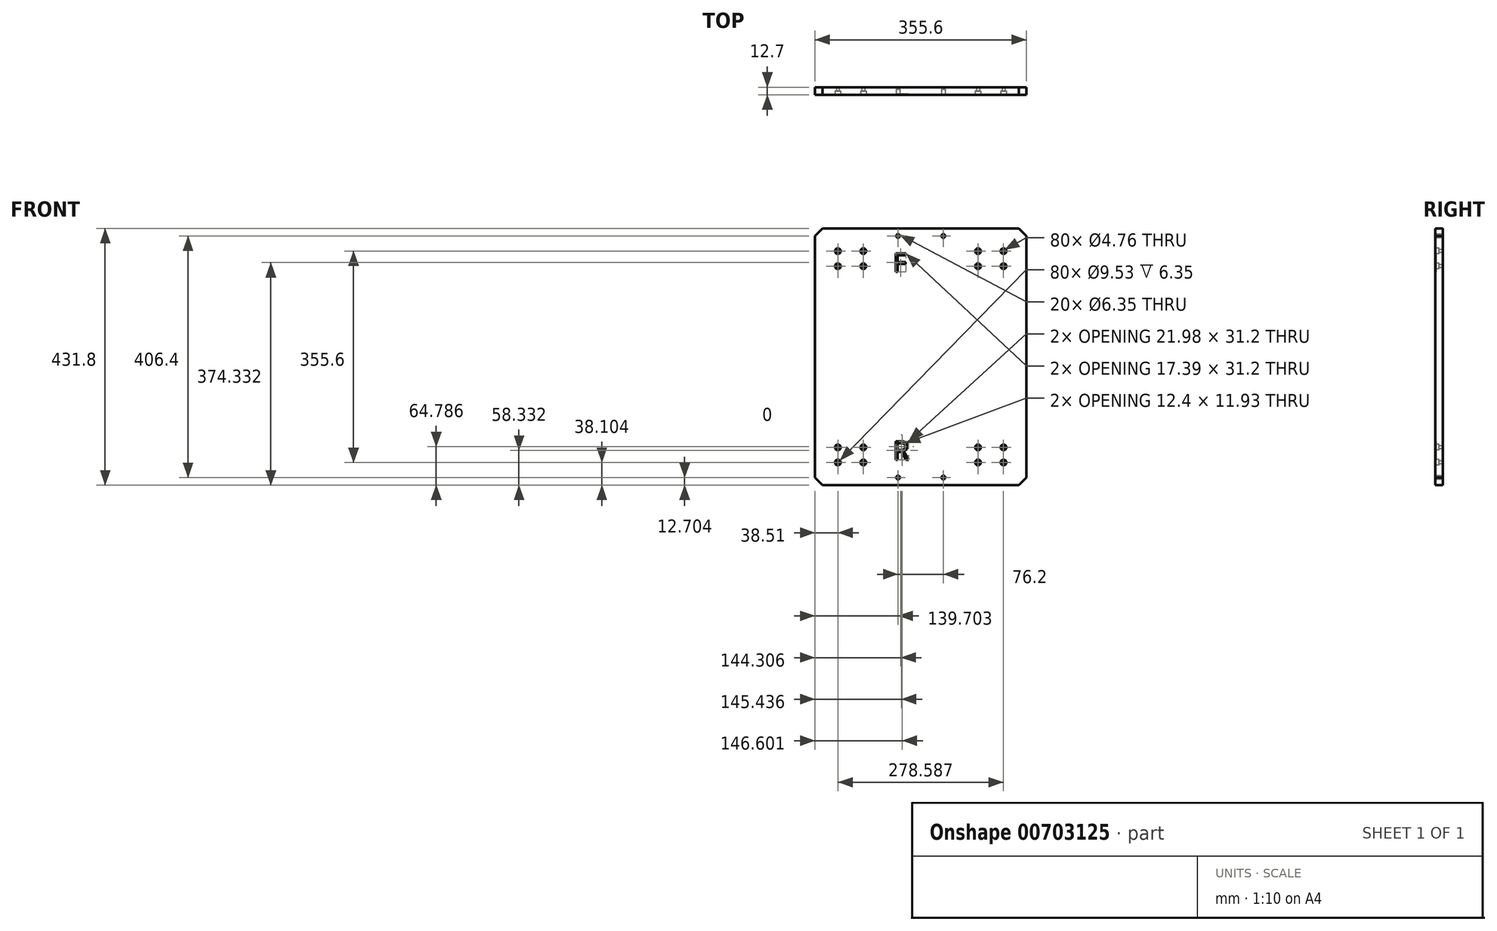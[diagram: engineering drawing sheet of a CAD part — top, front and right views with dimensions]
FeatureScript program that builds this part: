
annotation { "Feature Type Name" : "Feature", "Feature Type Description" : "" }
export const myFeature = defineFeature(function(context is Context, id is Id, definition is map)
    precondition{}
    {
        {
            var Q0;
            Q0=qCreatedBy(makeId("Front.planeOp"),FACE);
            var sketch = newSketch(context, id + "F0", { "sketchPlane" : qUnion([Q0])});
            skLineSegment(sketch, "E0.bottom", {"start": v(-223.94, -202.15) * mm, "end": v(131.66, -202.15) * mm});
            skLineSegment(sketch, "E0.top", {"start": v(-223.94, 229.65) * mm, "end": v(131.66, 229.65) * mm});
            skLineSegment(sketch, "E0.left", {"start": v(-223.94, -202.15) * mm, "end": v(-223.94, 229.65) * mm});
            skLineSegment(sketch, "E0.right", {"start": v(131.66, -202.15) * mm, "end": v(131.66, 229.65) * mm});
            skSolve(sketch);
        }
        {
            var Q0;
            Q0=makeQuery(id+"F0.imprint","IMPRINT",FACE,{"disambiguationData":[TD([[makeQuery(id+"F0.imprint","IMPRINT",EDGE,{"derivedFrom":sQuery(id+"F0.wireOp",EDGE,"E0.bottom")}),1.0]])]});
            extrude(context, id + "F1", {"entities" : qUnion([Q0]), "depth" : 12.7 * mm, "offsetDistance" : 25.4 * mm});
        }
        {
            var Q0;
            Q0=makeQuery(id+"F1.opExtrude","SWEPT_EDGE",EDGE,{"disambiguationData":[OSD([sQuery(id+"F0.wireOp",EDGE,"E0.top"),sQuery(id+"F0.wireOp",EDGE,"E0.left")])]});
            var Q1;
            Q1=makeQuery(id+"F1.opExtrude","SWEPT_EDGE",EDGE,{"disambiguationData":[OSD([sQuery(id+"F0.wireOp",EDGE,"E0.top"),sQuery(id+"F0.wireOp",EDGE,"E0.right")])]});
            var Q2;
            Q2=makeQuery(id+"F1.opExtrude","SWEPT_EDGE",EDGE,{"disambiguationData":[OSD([sQuery(id+"F0.wireOp",EDGE,"E0.bottom"),sQuery(id+"F0.wireOp",EDGE,"E0.right")])]});
            var Q3;
            Q3=makeQuery(id+"F1.opExtrude","SWEPT_EDGE",EDGE,{"disambiguationData":[OSD([sQuery(id+"F0.wireOp",EDGE,"E0.bottom"),sQuery(id+"F0.wireOp",EDGE,"E0.left")])]});
            chamfer(context, id + "F2", {"entities" : qUnion([Q0, Q1, Q2, Q3]), "chamferType" : ChamferType.OFFSET_ANGLE, "width" : 12.7 * mm, "oppositeDirection" : false, "angle" : 45 * degree, "tangentPropagation" : true});
        }
        {
            var Q0;
            Q0=makeQuery(id+"F1.opExtrude","CAP_FACE",FACE,{"disambiguationData":[OSD([sQuery(id+"F0.wireOp",EDGE,"E0.bottom"),sQuery(id+"F0.wireOp",EDGE,"E0.top"),sQuery(id+"F0.wireOp",EDGE,"E0.left"),sQuery(id+"F0.wireOp",EDGE,"E0.right")])],"isStart":false});
            var sketch = newSketch(context, id + "F3", { "sketchPlane" : qUnion([Q0])});
            skPoint(sketch, "E1", {"position": v(-185.43, -164.05) * mm});
            skPoint(sketch, "E2", {"position": v(-185.43, -138.65) * mm});
            skPoint(sketch, "E3.1.0.0", {"position": v(-142.56, -164.05) * mm});
            skLineSegment(sketch, "E3.direction1", {"start": v(-185.43, -164.05) * mm, "end": v(-142.56, -164.05) * mm, "construction": true});
            skPoint(sketch, "E4", {"position": v(-142.56, -138.65) * mm});
            skPoint(sketch, "E5", {"position": v(-46.14, 229.65) * mm});
            skLineSegment(sketch, "E6", {"start": v(-46.14, 229.65) * mm, "end": v(-46.14, -202.15) * mm, "construction": true});
            skPoint(sketch, "E7.MirrorP", {"position": v(50.28, -138.65) * mm});
            skPoint(sketch, "E8.MirrorP", {"position": v(93.16, -138.65) * mm});
            skPoint(sketch, "E9.MirrorP", {"position": v(93.16, -164.05) * mm});
            skPoint(sketch, "E10.MirrorP", {"position": v(50.28, -164.05) * mm});
            skLineSegment(sketch, "E11", {"start": v(-223.94, 13.75) * mm, "end": v(131.66, 13.75) * mm, "construction": true});
            skPoint(sketch, "E12.MirrorP", {"position": v(-185.43, 166.15) * mm});
            skPoint(sketch, "E13.MirrorP", {"position": v(-142.56, 166.15) * mm});
            skPoint(sketch, "E14.MirrorP", {"position": v(-142.56, 191.55) * mm});
            skPoint(sketch, "E15.MirrorP", {"position": v(-185.43, 191.55) * mm});
            skPoint(sketch, "E16.MirrorP", {"position": v(50.28, 166.15) * mm});
            skPoint(sketch, "E17.MirrorP", {"position": v(93.16, 166.15) * mm});
            skPoint(sketch, "E18.MirrorP", {"position": v(93.16, 191.55) * mm});
            skPoint(sketch, "E19.MirrorP", {"position": v(50.28, 191.55) * mm});
            skSolve(sketch);
        }
        {
            var Q0;
            Q0=sQuery(id+"F3.wireOp",VERTEX,"E12.MirrorP");
            var Q1;
            Q1=sQuery(id+"F3.wireOp",VERTEX,"E13.MirrorP");
            var Q2;
            Q2=sQuery(id+"F3.wireOp",VERTEX,"E14.MirrorP");
            var Q3;
            Q3=sQuery(id+"F3.wireOp",VERTEX,"E15.MirrorP");
            var Q4;
            Q4=sQuery(id+"F3.wireOp",VERTEX,"E16.MirrorP");
            var Q5;
            Q5=sQuery(id+"F3.wireOp",VERTEX,"E1");
            var Q6;
            Q6=sQuery(id+"F3.wireOp",VERTEX,"E2");
            var Q7;
            Q7=sQuery(id+"F3.wireOp",VERTEX,"E17.MirrorP");
            var Q8;
            Q8=sQuery(id+"F3.wireOp",VERTEX,"E18.MirrorP");
            var Q9;
            Q9=sQuery(id+"F3.wireOp",VERTEX,"E3.1.0.0");
            var Q10;
            Q10=sQuery(id+"F3.wireOp",VERTEX,"E7.MirrorP");
            var Q11;
            Q11=sQuery(id+"F3.wireOp",VERTEX,"E19.MirrorP");
            var Q12;
            Q12=sQuery(id+"F3.wireOp",VERTEX,"E4");
            var Q13;
            Q13=sQuery(id+"F3.wireOp",VERTEX,"E8.MirrorP");
            var Q14;
            Q14=sQuery(id+"F3.wireOp",VERTEX,"E9.MirrorP");
            var Q15;
            Q15=sQuery(id+"F3.wireOp",VERTEX,"E10.MirrorP");
            var Q16;
            Q16=makeQuery(id+"F1.opExtrude","SWEPT_BODY",BODY,{"disambiguationData":[OSD([sQuery(id+"F0.wireOp",EDGE,"E0.bottom"),sQuery(id+"F0.wireOp",EDGE,"E0.top"),sQuery(id+"F0.wireOp",EDGE,"E0.left"),sQuery(id+"F0.wireOp",EDGE,"E0.right")])]});
            hole(context, id + "F4", {"style" : HoleStyle.C_BORE, "endStyle" : HoleEndStyle.THROUGH, "holeDiameter" : 4.76 * mm, "cBoreDiameter" : 9.52 * mm, "cBoreDepth" : 6.35 * mm, "majorDiameter" : 6.35 * mm, "isTappedThrough" : true, "tappedDepth" : 12.7 * mm, "tapClearance" : 3, "locations" : qUnion([Q0, Q1, Q2, Q3, Q4, Q5, Q6, Q7, Q8, Q9, Q10, Q11, Q12, Q13, Q14, Q15]), "scope" : qUnion([Q16])});
        }
        {
            var Q0;
            Q0=makeQuery(id+"F1.opExtrude","CAP_FACE",FACE,{"disambiguationData":[OSD([sQuery(id+"F0.wireOp",EDGE,"E0.bottom"),sQuery(id+"F0.wireOp",EDGE,"E0.top"),sQuery(id+"F0.wireOp",EDGE,"E0.left"),sQuery(id+"F0.wireOp",EDGE,"E0.right")])],"isStart":false});
            var sketch = newSketch(context, id + "F5", { "sketchPlane" : qUnion([Q0])});
            skPoint(sketch, "E20", {"position": v(-84.24, -189.45) * mm});
            skPoint(sketch, "E21", {"position": v(-8.04, -189.45) * mm});
            skLineSegment(sketch, "E22", {"start": v(-223.94, 13.75) * mm, "end": v(131.66, 13.75) * mm, "construction": true});
            skPoint(sketch, "E23.MirrorP", {"position": v(-84.24, 216.95) * mm});
            skPoint(sketch, "E24.MirrorP", {"position": v(-8.04, 216.95) * mm});
            skSolve(sketch);
        }
        {
            var Q0;
            Q0=sQuery(id+"F5.wireOp",VERTEX,"E23.MirrorP");
            var Q1;
            Q1=sQuery(id+"F5.wireOp",VERTEX,"E24.MirrorP");
            var Q2;
            Q2=sQuery(id+"F5.wireOp",VERTEX,"E21");
            var Q3;
            Q3=sQuery(id+"F5.wireOp",VERTEX,"E20");
            var Q4;
            Q4=makeQuery(id+"F1.opExtrude","SWEPT_BODY",BODY,{"disambiguationData":[OSD([sQuery(id+"F0.wireOp",EDGE,"E0.bottom"),sQuery(id+"F0.wireOp",EDGE,"E0.top"),sQuery(id+"F0.wireOp",EDGE,"E0.left"),sQuery(id+"F0.wireOp",EDGE,"E0.right")])]});
            hole(context, id + "F6", {"style" : HoleStyle.SIMPLE, "endStyle" : HoleEndStyle.BLIND, "holeDiameter" : 6.35 * mm, "majorDiameter" : 6.35 * mm, "holeDepth" : 9.52 * mm, "isTappedThrough" : true, "tappedDepth" : 12.7 * mm, "tapClearance" : 3, "locations" : qUnion([Q0, Q1, Q2, Q3]), "scope" : qUnion([Q4])});
        }
        {
            var Q0;
            Q0=makeQuery(id+"F1.opExtrude","CAP_FACE",FACE,{"disambiguationData":[OSD([sQuery(id+"F0.wireOp",EDGE,"E0.bottom"),sQuery(id+"F0.wireOp",EDGE,"E0.top"),sQuery(id+"F0.wireOp",EDGE,"E0.left"),sQuery(id+"F0.wireOp",EDGE,"E0.right")])],"isStart":false});
            var sketch = newSketch(context, id + "F7", { "sketchPlane" : qUnion([Q0])});
            skText(sketch, "E25", { "text": "F\n\n", "fontName": "OpenSans-Regular.ttf"});
            skText(sketch, "E26", { "text": "R\n", "fontName": "OpenSans-Regular.ttf"});
            const initialGuessF7  = {"E25": [-0.09262, 0.15658, 1, 0, 0.03147], "E26": [-0.09262, -0.15942, 1, 0, 0.03147]};
            skSetInitialGuess(sketch, initialGuessF7);
            skSolve(sketch);
        }
        {
            var Q0;
            Q0=qSketchRegion(id+"F7",true);
            extrude(context, id + "F8", {"entities" : qUnion([Q0]), "operationType" : NewBodyOperationType.REMOVE, "oppositeDirection" : true, "depth" : 1.27 * mm, "offsetDistance" : 25.4 * mm});
        }
    });
